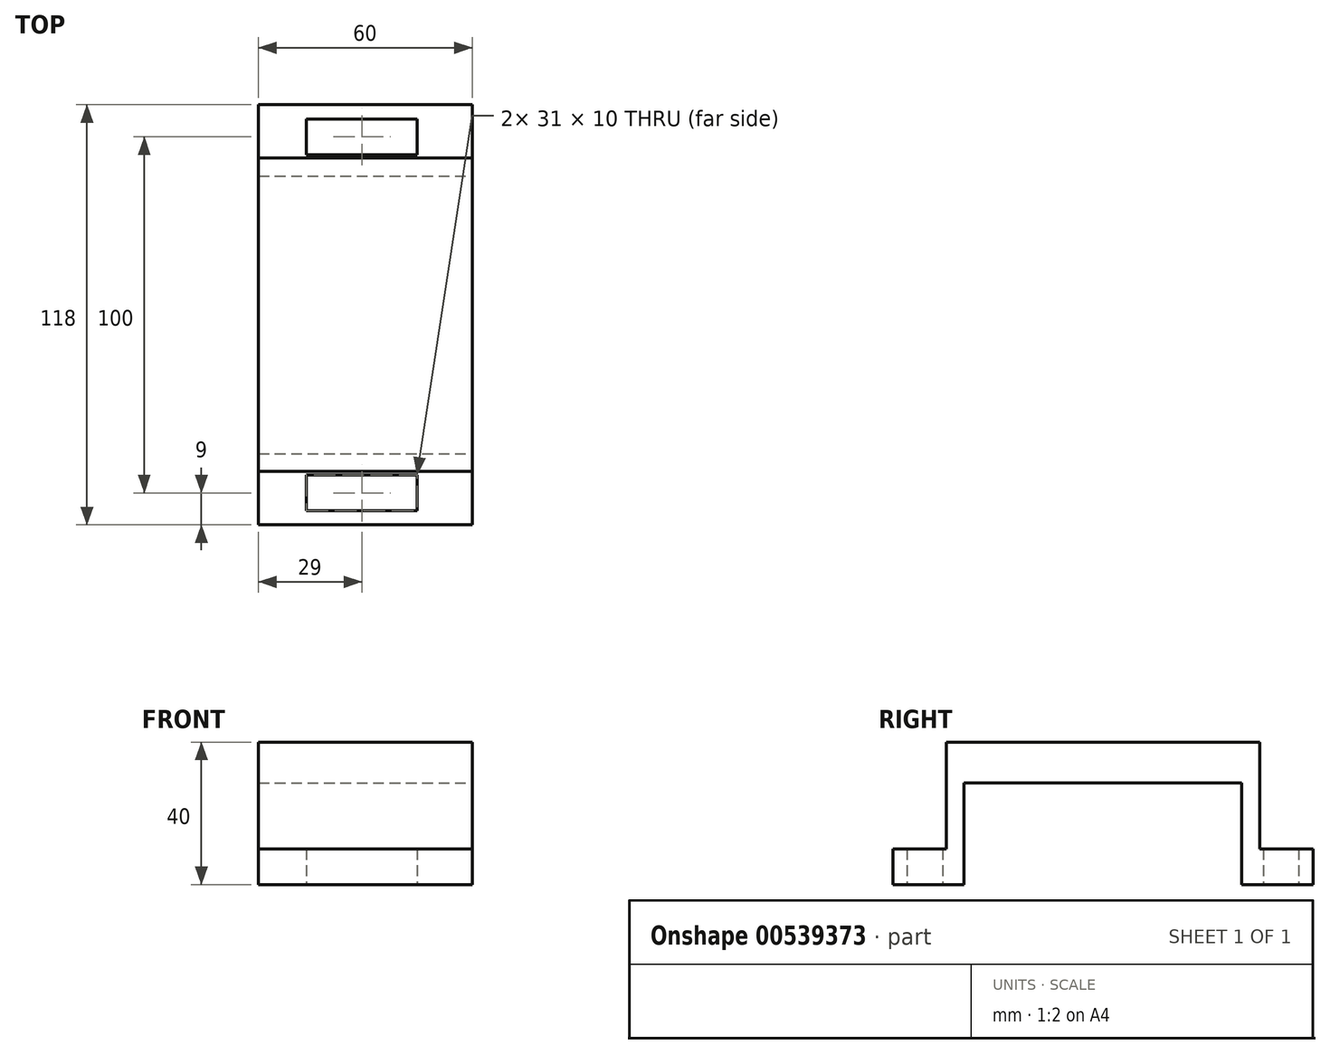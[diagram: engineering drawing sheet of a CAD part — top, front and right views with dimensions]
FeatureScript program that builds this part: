
annotation { "Feature Type Name" : "Feature", "Feature Type Description" : "" }
export const myFeature = defineFeature(function(context is Context, id is Id, definition is map)
    precondition{}
    {
        {
            var Q0;
            Q0=qCreatedBy(makeId("Top.planeOp"),FACE);
            var sketch = newSketch(context, id + "F0", { "sketchPlane" : qUnion([Q0])});
            skLineSegment(sketch, "E0.bottom", {"start": v(-30, 44) * mm, "end": v(30, 44) * mm});
            skLineSegment(sketch, "E0.top", {"start": v(-30, -44) * mm, "end": v(30, -44) * mm});
            skLineSegment(sketch, "E0.left", {"start": v(-30, 44) * mm, "end": v(-30, -44) * mm});
            skLineSegment(sketch, "E0.right", {"start": v(30, 44) * mm, "end": v(30, -44) * mm});
            skSolve(sketch);
        }
        {
            var Q0;
            Q0=makeQuery(id+"F0.imprint","IMPRINT",FACE,{"disambiguationData":[TD([[makeQuery(id+"F0.imprint","IMPRINT",EDGE,{"derivedFrom":sQuery(id+"F0.wireOp",EDGE,"E0.bottom")}),-1.0]])]});
            extrude(context, id + "F1", {"entities" : qUnion([Q0]), "depth" : 40 * mm, "offsetDistance" : 25 * mm});
        }
        {
            var Q0;
            Q0=qCreatedBy(makeId("Top.planeOp"),FACE);
            var sketch = newSketch(context, id + "F2", { "sketchPlane" : qUnion([Q0])});
            skLineSegment(sketch, "E1.bottom", {"start": v(-50.7, 39) * mm, "end": v(30, 39) * mm});
            skLineSegment(sketch, "E1.top", {"start": v(-50.7, -39) * mm, "end": v(30, -39) * mm});
            skLineSegment(sketch, "E1.left", {"start": v(-50.7, 39) * mm, "end": v(-50.7, -39) * mm});
            skLineSegment(sketch, "E1.right", {"start": v(30, 39) * mm, "end": v(30, -39) * mm});
            skSolve(sketch);
        }
        {
            var Q0;
            Q0 = qSketchRegion(id + "F2", true);
            extrude(context, id + "F3", {"entities" : qUnion([Q0]), "operationType" : NewBodyOperationType.REMOVE, "depth" : 28.5 * mm, "offsetDistance" : 25 * mm});
        }
        {
            var Q0;
            Q0=qCreatedBy(makeId("Front.planeOp"),FACE);
            cPlane(context, id + "F4", {"entities" : qUnion([Q0]), "cplaneType" : CPlaneType.OFFSET, "offset" : 44 * mm, "width" : 150 * mm, "height" : 150 * mm});
        }
        {
            var Q0;
            Q0=qCreatedBy(id+"F4.planeOp",FACE);
            var sketch = newSketch(context, id + "F5", { "sketchPlane" : qUnion([Q0])});
            skLineSegment(sketch, "E2.bottom", {"start": v(-30, 10) * mm, "end": v(30, 10) * mm});
            skLineSegment(sketch, "E2.top", {"start": v(-30, 0) * mm, "end": v(30, 0) * mm});
            skLineSegment(sketch, "E2.left", {"start": v(-30, 10) * mm, "end": v(-30, 0) * mm});
            skLineSegment(sketch, "E2.right", {"start": v(30, 10) * mm, "end": v(30, 0) * mm});
            skSolve(sketch);
        }
        {
            var Q0;
            Q0 = qSketchRegion(id + "F5", true);
            extrude(context, id + "F6", {"entities" : qUnion([Q0]), "operationType" : NewBodyOperationType.ADD, "depth" : 15 * mm, "offsetDistance" : 25 * mm});
        }
        {
            var Q0;
            Q0=qCreatedBy(makeId("Front.planeOp"),FACE);
            cPlane(context, id + "F7", {"entities" : qUnion([Q0]), "cplaneType" : CPlaneType.OFFSET, "offset" : 44 * mm, "oppositeDirection" : true, "width" : 150 * mm, "height" : 150 * mm});
        }
        {
            var Q0;
            Q0=qCreatedBy(id+"F7.planeOp",FACE);
            var sketch = newSketch(context, id + "F8", { "sketchPlane" : qUnion([Q0])});
            skLineSegment(sketch, "E3.bottom", {"start": v(30, 10) * mm, "end": v(-30, 10) * mm});
            skLineSegment(sketch, "E3.top", {"start": v(30, 0) * mm, "end": v(-30, 0) * mm});
            skLineSegment(sketch, "E3.left", {"start": v(30, 10) * mm, "end": v(30, 0) * mm});
            skLineSegment(sketch, "E3.right", {"start": v(-30, 10) * mm, "end": v(-30, 0) * mm});
            skSolve(sketch);
        }
        {
            var Q0;
            Q0 = qSketchRegion(id + "F8", true);
            extrude(context, id + "F9", {"entities" : qUnion([Q0]), "operationType" : NewBodyOperationType.ADD, "oppositeDirection" : true, "depth" : 15 * mm, "offsetDistance" : 25 * mm});
        }
        {
            var Q0;
            Q0=qCreatedBy(makeId("Top.planeOp"),FACE);
            var sketch = newSketch(context, id + "F10", { "sketchPlane" : qUnion([Q0])});
            skLineSegment(sketch, "E4.bottom", {"start": v(14.5, -55) * mm, "end": v(-16.5, -55) * mm});
            skLineSegment(sketch, "E4.top", {"start": v(14.5, -45) * mm, "end": v(-16.5, -45) * mm});
            skLineSegment(sketch, "E4.left", {"start": v(14.5, -55) * mm, "end": v(14.5, -45) * mm});
            skLineSegment(sketch, "E4.right", {"start": v(-16.5, -55) * mm, "end": v(-16.5, -45) * mm});
            skLineSegment(sketch, "E5.bottom", {"start": v(14.5, 45) * mm, "end": v(-16.5, 45) * mm});
            skLineSegment(sketch, "E5.top", {"start": v(14.5, 55) * mm, "end": v(-16.5, 55) * mm});
            skLineSegment(sketch, "E5.left", {"start": v(14.5, 45) * mm, "end": v(14.5, 55) * mm});
            skLineSegment(sketch, "E5.right", {"start": v(-16.5, 45) * mm, "end": v(-16.5, 55) * mm});
            skSolve(sketch);
        }
        {
            var Q0;
            Q0 = qSketchRegion(id + "F10", true);
            extrude(context, id + "F11", {"entities" : qUnion([Q0]), "operationType" : NewBodyOperationType.REMOVE, "depth" : 25 * mm, "offsetDistance" : 25 * mm});
        }
    });
